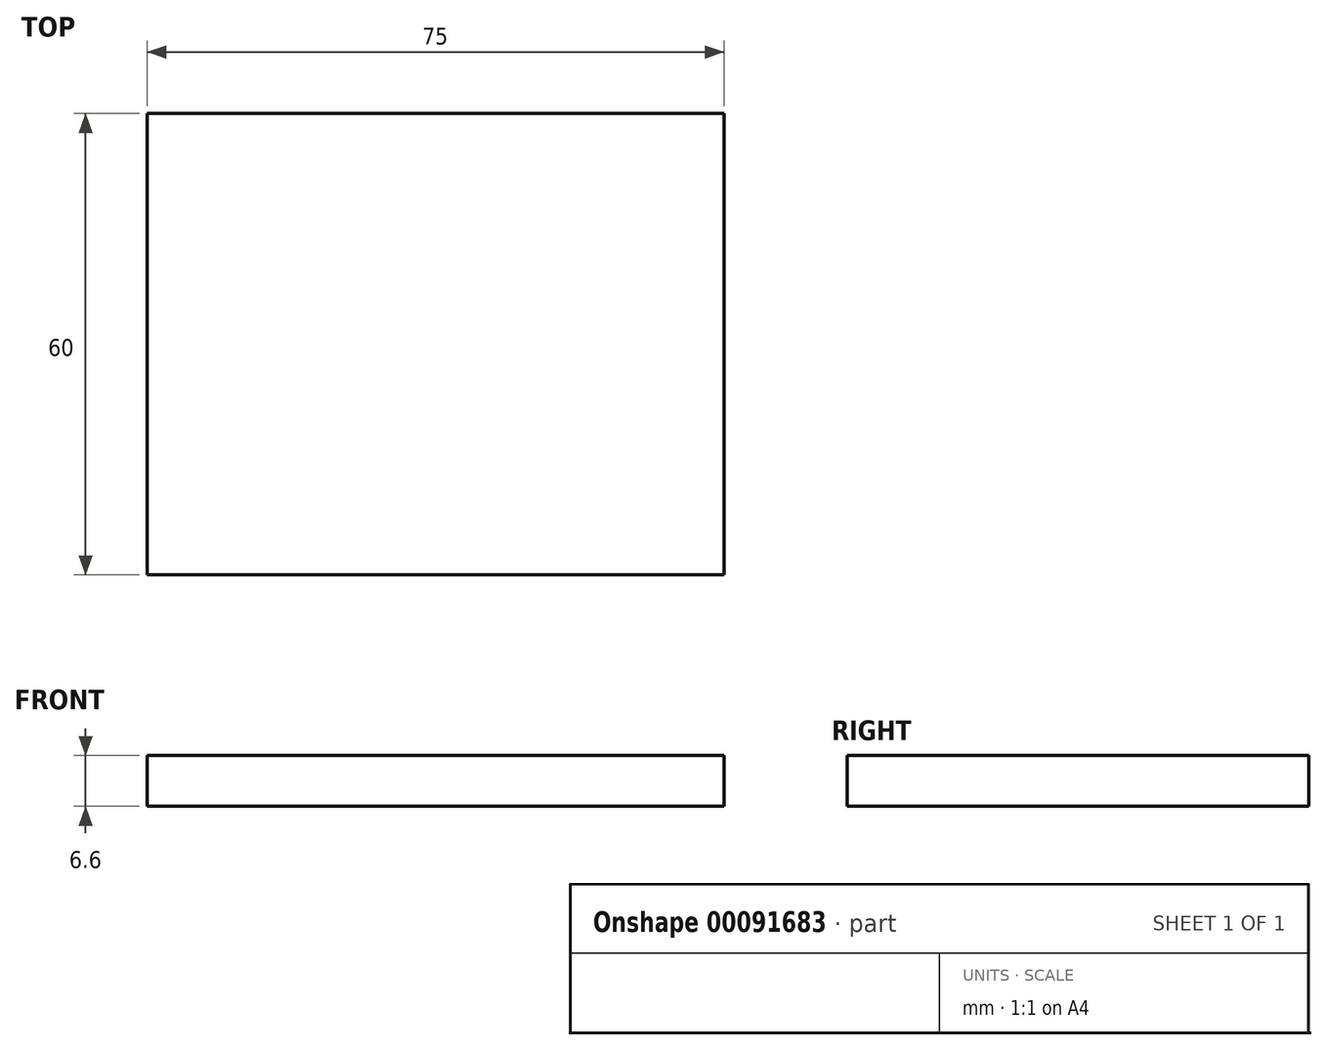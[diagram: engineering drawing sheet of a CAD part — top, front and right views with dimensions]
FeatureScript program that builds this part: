
annotation { "Feature Type Name" : "Feature", "Feature Type Description" : "" }
export const myFeature = defineFeature(function(context is Context, id is Id, definition is map)
    precondition{}
    {
        {
            var Q0;
            Q0=qCreatedBy(makeId("Top.planeOp"),FACE);
            var sketch = newSketch(context, id + "F0", { "sketchPlane" : qUnion([Q0])});
            skLineSegment(sketch, "E0.bottom", {"start": v(37.5, 30) * mm, "end": v(-37.5, 30) * mm});
            skLineSegment(sketch, "E0.top", {"start": v(37.5, -30) * mm, "end": v(-37.5, -30) * mm});
            skLineSegment(sketch, "E0.left", {"start": v(37.5, 30) * mm, "end": v(37.5, -30) * mm});
            skLineSegment(sketch, "E0.right", {"start": v(-37.5, 30) * mm, "end": v(-37.5, -30) * mm});
            skPoint(sketch, "E0.middle", {"position": v(0, 0) * mm});
            skSolve(sketch);
        }
        {
            var Q0;
            Q0=makeQuery(id+"F0.imprint","IMPRINT",FACE,{"disambiguationData":[TD([[makeQuery(id+"F0.imprint","IMPRINT",EDGE,{"derivedFrom":sQuery(id+"F0.wireOp",EDGE,"E0.bottom")}),1.0]])]});
            extrude(context, id + "F1", {"entities" : qUnion([Q0]), "depth" : 6.6 * mm});
        }
    });
